# Revit family: Haworth_ToDo_Chair_Single
name_source: partatom
category: Furniture
revit_build: Autodesk Revit 2018 (Build: 20170223_1515(x64)
units: mm (PartAtom-declared; Revit-internal decimal feet)

## family parameters
Always vertical = Yes
Cut with Voids When Loaded = No
OmniClass Number = 23.40.70.14.64.11
OmniClass Title = Office Furniture
Room Calculation Point = No
Shared = No
Work Plane-Based = No

## types (2) — shared parameters
Assembly Code = E2020200
Caster Finish = Haworth _ Polymer _ Black
Manufacturer = Haworth
Model = Haworth - Chair - ToDo - Single
Revision = 2
Shelf Finish = Haworth _ Wood _ Light Maple
Size = Verify Final Dim. w/ Haworth
Sustainability Info = http://www.haworth.com
Table Finish = Haworth _ Wood _ Light Maple
Trim Finish = Haworth _ Paint _ Metallic Silver
URL = http://www.haworth.com
URL - Product = http://www.haworth.com
Warranty = http://www.haworth.com

## per-type parameters (varying)
| type | Cup Holder | Description | Grommet | Handle | Mobile | Shelf | Stationary | Tablet |
| TQ84 - 0011 - Fully Loaded | Yes | Haworth - Chair - ToDo - Single - Fully Loaded - 29.25d x 30w x 31.25h | Yes | Yes | Yes | Yes | No | Yes |
| TQ84 - 0011 - Plain | No | Haworth - Chair - ToDo - Single - Plain - 29.25d x 30w x 31.25h | No | No | No | No | Yes | No |

## geometry (parser evidence)
native form markers: Sweep x5
no freeform markers — native parametric forms only
